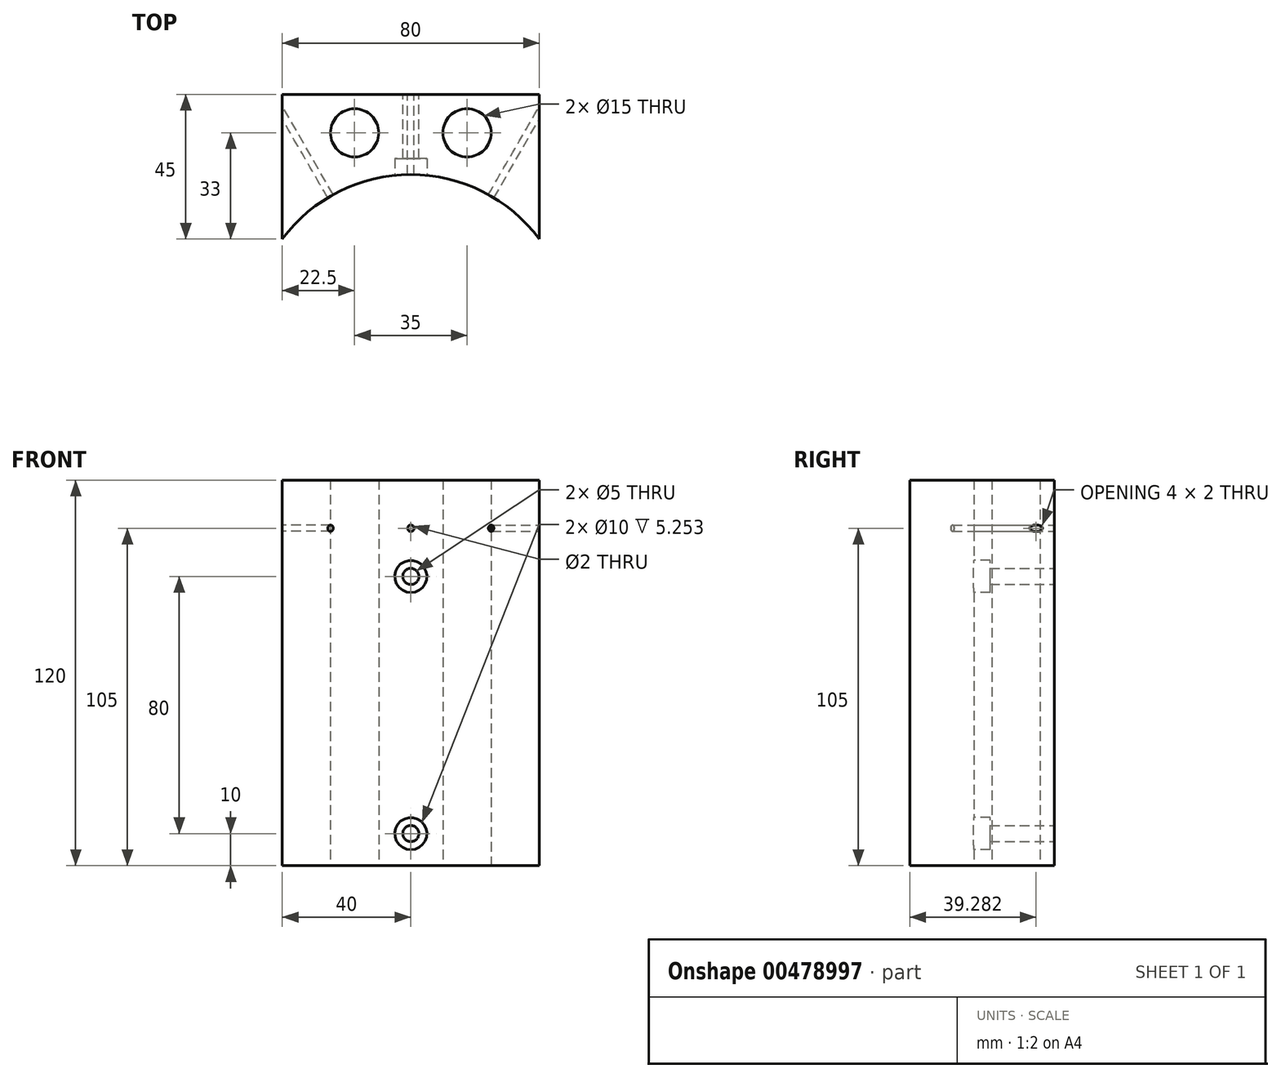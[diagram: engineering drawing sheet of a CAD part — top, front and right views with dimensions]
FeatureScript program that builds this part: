
annotation { "Feature Type Name" : "Feature", "Feature Type Description" : "" }
export const myFeature = defineFeature(function(context is Context, id is Id, definition is map)
    precondition{}
    {
        {
            var Q0;
            Q0=qCreatedBy(makeId("Front.planeOp"),FACE);
            var sketch = newSketch(context, id + "F0", { "sketchPlane" : qUnion([Q0])});
            skPoint(sketch, "E0.middle", {"position": v(0, 0) * mm});
            skCircle(sketch, "E1", {"center": v(0, 30) * mm, "radius": 2.5 * mm});
            skLineSegment(sketch, "E2", {"start": v(0, 99.7) * mm, "end": v(0, -99.7) * mm, "construction": true});
            skCircle(sketch, "E3", {"center": v(0, -50) * mm, "radius": 2.5 * mm});
            skLineSegment(sketch, "E4.bottom", {"start": v(40, 60) * mm, "end": v(-40, 60) * mm});
            skLineSegment(sketch, "E4.top", {"start": v(40, -60) * mm, "end": v(-40, -60) * mm});
            skLineSegment(sketch, "E4.left", {"start": v(40, 60) * mm, "end": v(40, -60) * mm});
            skLineSegment(sketch, "E4.right", {"start": v(-40, 60) * mm, "end": v(-40, -60) * mm});
            skCircle(sketch, "E5", {"center": v(0, 45) * mm, "radius": 1 * mm});
            skSolve(sketch);
        }
        {
            var Q0;
            Q0 = qSketchRegion(id + "F0", true);
            extrude(context, id + "F1", {"entities" : qUnion([Q0]), "depth" : 50 * mm});
        }
        {
            var Q0;
            Q0=makeQuery(id+"F1.opExtrude","SWEPT_FACE",FACE,{"disambiguationData":[OSD([sQuery(id+"F0.wireOp",EDGE,"E4.top")])]});
            var sketch = newSketch(context, id + "F2", { "sketchPlane" : qUnion([Q0])});
            skLineSegment(sketch, "E6", {"start": v(0, 53.77) * mm, "end": v(0, -11.36) * mm, "construction": true});
            skPoint(sketch, "E7", {"position": v(0, 25) * mm});
            skArc(sketch, "E8", {"start": v(-43.3, 50) * mm, "mid": v(0, 25) * mm, "end": v(43.3, 50) * mm});
            skLineSegment(sketch, "E9.0", {"start": v(43.3, 50) * mm, "end": v(-43.3, 50) * mm});
            skPoint(sketch, "E10.orphan", {"position": v(40, 50) * mm});
            skPoint(sketch, "E11.orphan", {"position": v(-40, 50) * mm});
            skSolve(sketch);
        }
        {
            var Q0;
            Q0 = qSketchRegion(id + "F2", true);
            extrude(context, id + "F3", {"entities" : qUnion([Q0]), "operationType" : NewBodyOperationType.REMOVE, "endBound" : BoundingType.THROUGH_ALL, "oppositeDirection" : true, "depth" : 25 * mm});
        }
        {
            var Q0;
            Q0=qCreatedBy(makeId("Front.planeOp"),FACE);
            cPlane(context, id + "F4", {"entities" : qUnion([Q0]), "cplaneType" : CPlaneType.OFFSET, "offset" : 30 * mm, "width" : 150 * mm, "height" : 150 * mm});
        }
        {
            var Q0;
            Q0=qCreatedBy(id+"F4.planeOp",FACE);
            var sketch = newSketch(context, id + "F5", { "sketchPlane" : qUnion([Q0])});
            skCircle(sketch, "E12", {"center": v(0, -50) * mm, "radius": 5 * mm});
            skCircle(sketch, "E13", {"center": v(0, 30) * mm, "radius": 5 * mm});
            skSolve(sketch);
        }
        {
            var Q0;
            Q0 = qSketchRegion(id + "F5", true);
            extrude(context, id + "F6", {"entities" : qUnion([Q0]), "operationType" : NewBodyOperationType.REMOVE, "oppositeDirection" : true, "depth" : 10 * mm});
        }
        {
            var Q0;
            Q0=makeQuery(id+"F1.opExtrude","SWEPT_FACE",FACE,{"disambiguationData":[OSD([sQuery(id+"F0.wireOp",EDGE,"E4.top")])]});
            var sketch = newSketch(context, id + "F7", { "sketchPlane" : qUnion([Q0])});
            skCircle(sketch, "E14", {"center": v(-17.5, 12) * mm, "radius": 7.5 * mm});
            skCircle(sketch, "E15.MirrorC", {"center": v(17.5, 12) * mm, "radius": 7.5 * mm});
            skSolve(sketch);
        }
        {
            var Q0;
            Q0 = qSketchRegion(id + "F7", true);
            extrude(context, id + "F8", {"entities" : qUnion([Q0]), "operationType" : NewBodyOperationType.REMOVE, "endBound" : BoundingType.UP_TO_NEXT, "oppositeDirection" : true, "depth" : 25 * mm});
        }
        {
            var Q0;
            Q0=makeQuery(id+"F1.opExtrude","SWEPT_FACE",FACE,{"disambiguationData":[OSD([sQuery(id+"F0.wireOp",EDGE,"E4.bottom")])]});
            cPlane(context, id + "F9", {"entities" : qUnion([Q0]), "cplaneType" : CPlaneType.OFFSET, "offset" : 15 * mm, "oppositeDirection" : true, "width" : 150 * mm, "height" : 150 * mm});
        }
        {
            var Q0;
            Q0=qCreatedBy(id+"F9.planeOp",FACE);
            var sketch = newSketch(context, id + "F10", { "sketchPlane" : qUnion([Q0])});
            skPoint(sketch, "E16.0", {"position": v(0, 0) * mm});
            skLineSegment(sketch, "E17", {"start": v(0, 0) * mm, "end": v(0, -75) * mm, "construction": true});
            skLineSegment(sketch, "E18", {"start": v(0, -75) * mm, "end": v(50, 11.6) * mm, "construction": true});
            skLineSegment(sketch, "E19", {"start": v(0, -75) * mm, "end": v(-50, 11.6) * mm, "construction": true});
            skPoint(sketch, "E20", {"position": v(68.48, -60.2) * mm});
            skSolve(sketch);
        }
        {
            var Q0;
            Q0=sQuery(id+"F10.wireOp",VERTEX,"E18.end");
            var Q1;
            Q1=sQuery(id+"F10.wireOp",EDGE,"E18");
            cPlane(context, id + "F11", {"entities" : qUnion([Q0, Q1]), "cplaneType" : CPlaneType.LINE_POINT, "offset" : 25 * mm, "width" : 150 * mm, "height" : 150 * mm});
        }
        {
            var Q0;
            Q0=sQuery(id+"F10.wireOp",EDGE,"E19");
            var Q1;
            Q1=sQuery(id+"F10.wireOp",VERTEX,"E19.end");
            cPlane(context, id + "F12", {"entities" : qUnion([Q0, Q1]), "cplaneType" : CPlaneType.LINE_POINT, "offset" : 25 * mm, "width" : 150 * mm, "height" : 150 * mm});
        }
        {
            var Q0;
            Q0=qCreatedBy(id+"F11.planeOp",FACE);
            var sketch = newSketch(context, id + "F13", { "sketchPlane" : qUnion([Q0])});
            skPoint(sketch, "E21.0", {"position": v(-37.5, 45) * mm});
            skCircle(sketch, "E22", {"center": v(-37.5, 45) * mm, "radius": 1 * mm});
            skSolve(sketch);
        }
        {
            var Q0;
            Q0=qCreatedBy(id+"F12.planeOp",FACE);
            var sketch = newSketch(context, id + "F14", { "sketchPlane" : qUnion([Q0])});
            skPoint(sketch, "E23.0", {"position": v(37.5, 45) * mm});
            skCircle(sketch, "E24", {"center": v(37.5, 45) * mm, "radius": 1 * mm});
            skSolve(sketch);
        }
        {
            var Q0;
            Q0 = qSketchRegion(id + "F13", true);
            extrude(context, id + "F15", {"entities" : qUnion([Q0]), "operationType" : NewBodyOperationType.REMOVE, "endBound" : BoundingType.THROUGH_ALL, "oppositeDirection" : true, "depth" : 25 * mm});
        }
        {
            var Q0;
            Q0 = qSketchRegion(id + "F14", true);
            extrude(context, id + "F16", {"entities" : qUnion([Q0]), "operationType" : NewBodyOperationType.REMOVE, "endBound" : BoundingType.THROUGH_ALL, "oppositeDirection" : true, "depth" : 25 * mm});
        }
    });
